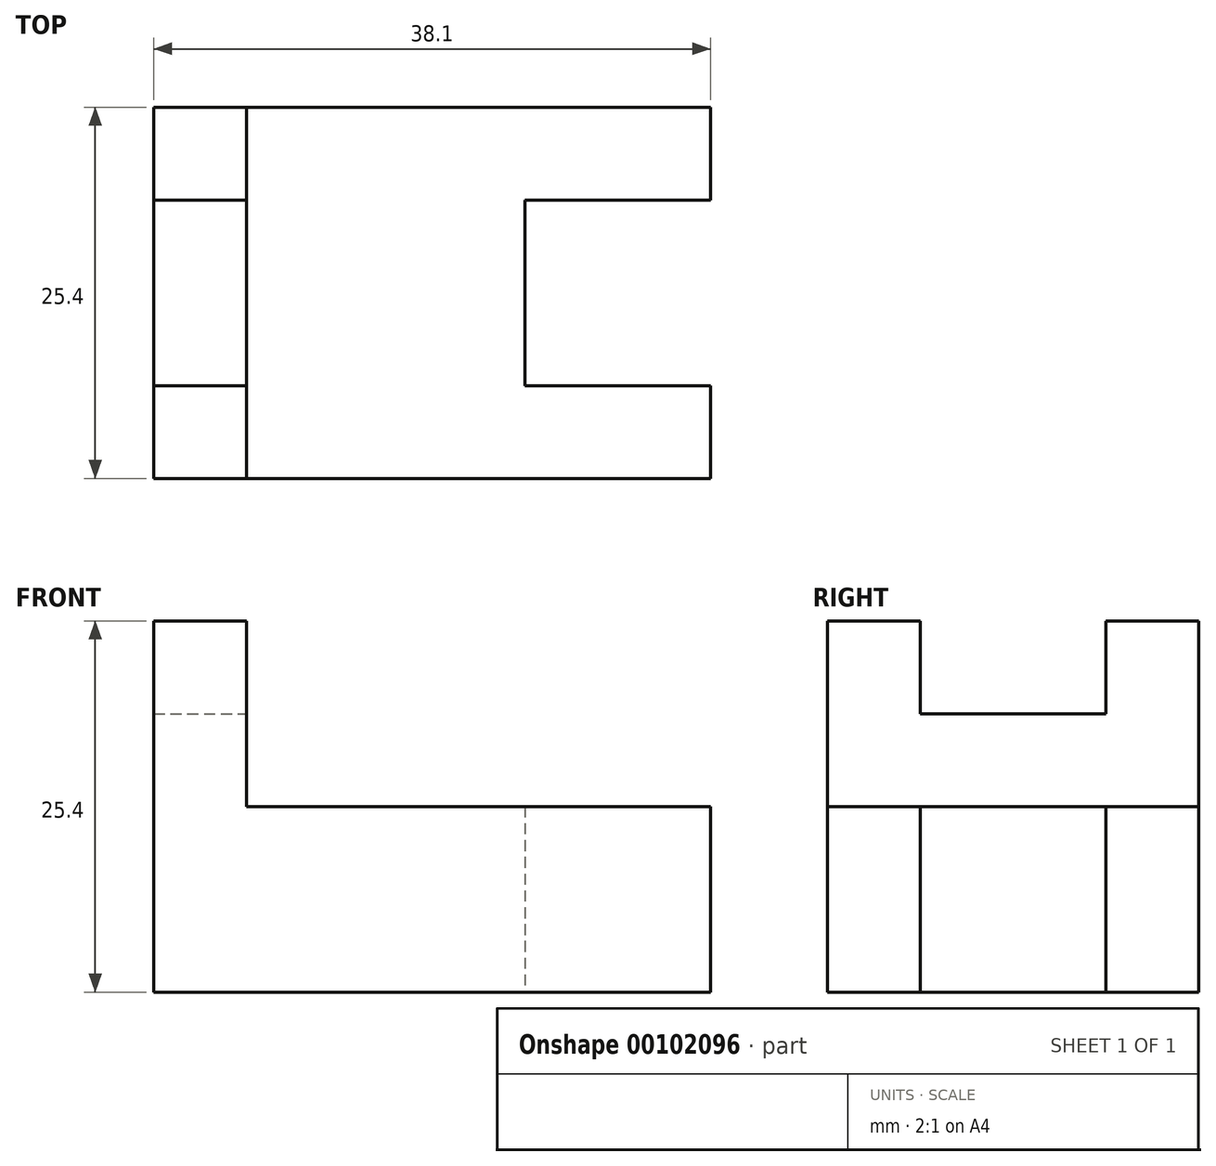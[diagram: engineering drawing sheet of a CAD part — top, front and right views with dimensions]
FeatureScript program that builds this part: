
annotation { "Feature Type Name" : "Feature", "Feature Type Description" : "" }
export const myFeature = defineFeature(function(context is Context, id is Id, definition is map)
    precondition{}
    {
        {
            var Q0;
            Q0=qCreatedBy(makeId("Top.planeOp"),FACE);
            var sketch = newSketch(context, id + "F0", { "sketchPlane" : qUnion([Q0])});
            skLineSegment(sketch, "E0", {"start": v(0, 25.4) * mm, "end": v(0, 0) * mm});
            skLineSegment(sketch, "E1", {"start": v(0, 0) * mm, "end": v(38.1, 0) * mm});
            skLineSegment(sketch, "E2", {"start": v(38.1, 0) * mm, "end": v(38.1, 6.35) * mm});
            skLineSegment(sketch, "E3", {"start": v(38.1, 6.35) * mm, "end": v(25.4, 6.35) * mm});
            skLineSegment(sketch, "E4", {"start": v(25.4, 6.35) * mm, "end": v(25.4, 19.05) * mm});
            skLineSegment(sketch, "E5", {"start": v(25.4, 19.05) * mm, "end": v(38.1, 19.05) * mm});
            skLineSegment(sketch, "E6", {"start": v(38.1, 19.05) * mm, "end": v(38.1, 25.4) * mm});
            skLineSegment(sketch, "E7", {"start": v(38.1, 25.4) * mm, "end": v(0, 25.4) * mm});
            skSolve(sketch);
        }
        {
            var Q0;
            Q0=makeQuery(id+"F0.imprint","IMPRINT",FACE,{"disambiguationData":[TD([[makeQuery(id+"F0.imprint","IMPRINT",EDGE,{"derivedFrom":sQuery(id+"F0.wireOp",EDGE,"E0")}),1.0]])]});
            extrude(context, id + "F1", {"entities" : qUnion([Q0]), "depth" : 12.7 * mm});
        }
        {
            var Q0;
            Q0=makeQuery(id+"F1.opExtrude","CAP_FACE",FACE,{"disambiguationData":[OSD([sQuery(id+"F0.wireOp",EDGE,"E0"),sQuery(id+"F0.wireOp",EDGE,"E1"),sQuery(id+"F0.wireOp",EDGE,"E2"),sQuery(id+"F0.wireOp",EDGE,"E3"),sQuery(id+"F0.wireOp",EDGE,"E4"),sQuery(id+"F0.wireOp",EDGE,"E5"),sQuery(id+"F0.wireOp",EDGE,"E6"),sQuery(id+"F0.wireOp",EDGE,"E7")])],"isStart":false});
            var sketch = newSketch(context, id + "F2", { "sketchPlane" : qUnion([Q0])});
            skLineSegment(sketch, "E8.bottom", {"start": v(0, 25.4) * mm, "end": v(6.35, 25.4) * mm});
            skLineSegment(sketch, "E8.top", {"start": v(0, 0) * mm, "end": v(6.35, 0) * mm});
            skLineSegment(sketch, "E8.left", {"start": v(0, 25.4) * mm, "end": v(0, 0) * mm});
            skLineSegment(sketch, "E8.right", {"start": v(6.35, 25.4) * mm, "end": v(6.35, 0) * mm});
            skSolve(sketch);
        }
        {
            var Q0;
            Q0 = qSketchRegion(id + "F2", true);
            extrude(context, id + "F3", {"entities" : qUnion([Q0]), "operationType" : NewBodyOperationType.ADD, "depth" : 12.7 * mm});
        }
        {
            var Q0;
            Q0=makeQuery(id+"F3.opExtrude","SWEPT_FACE",FACE,{"disambiguationData":[OSD([sQuery(id+"F2.wireOp",EDGE,"E8.right")])]});
            var sketch = newSketch(context, id + "F4", { "sketchPlane" : qUnion([Q0])});
            skLineSegment(sketch, "E9.bottom", {"start": v(6.35, 25.4) * mm, "end": v(19.05, 25.4) * mm});
            skLineSegment(sketch, "E9.top", {"start": v(6.35, 19.05) * mm, "end": v(19.05, 19.05) * mm});
            skLineSegment(sketch, "E9.left", {"start": v(6.35, 25.4) * mm, "end": v(6.35, 19.05) * mm});
            skLineSegment(sketch, "E9.right", {"start": v(19.05, 25.4) * mm, "end": v(19.05, 19.05) * mm});
            skSolve(sketch);
        }
        {
            var Q0;
            Q0=makeQuery(id+"F4.imprint","IMPRINT",FACE,{"disambiguationData":[TD([[makeQuery(id+"F4.imprint","IMPRINT",EDGE,{"derivedFrom":sQuery(id+"F4.wireOp",EDGE,"E9.bottom")}),1.0]])]});
            extrude(context, id + "F5", {"entities" : qUnion([Q0]), "operationType" : NewBodyOperationType.REMOVE, "oppositeDirection" : true, "depth" : 25.4 * mm});
        }
    });
